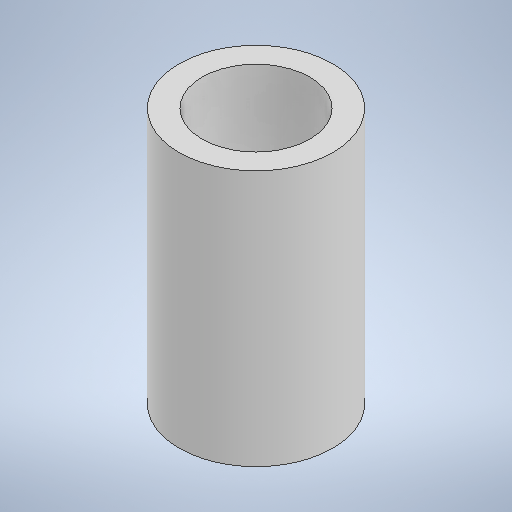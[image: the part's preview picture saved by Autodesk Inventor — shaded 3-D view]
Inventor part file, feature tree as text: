
AUTODESK INVENTOR PART (.ipt)
format: ipt  version: 2025.1 (Build 291241000, 241)  size: 518,144 bytes
history: native  units: in
note: dims shown in document units (in); Inventor stores cm internally (conversion verified against a paired STEP export)
features: extrude x1, sketch x1
ambient origin geometry x8: Origin, YZ Plane, XZ Plane, XY Plane, X Axis, Y Axis, Z Axis, Center Point
bodies: Solid1 (feature_tree)
feature tree (2):
  extrude  "Extrusion1"  Depth=0.3937in
  sketch  "Sketch1"  dims[d0=0.1654in d1=0.2362in d2=0.3937in d3=0.0in]
